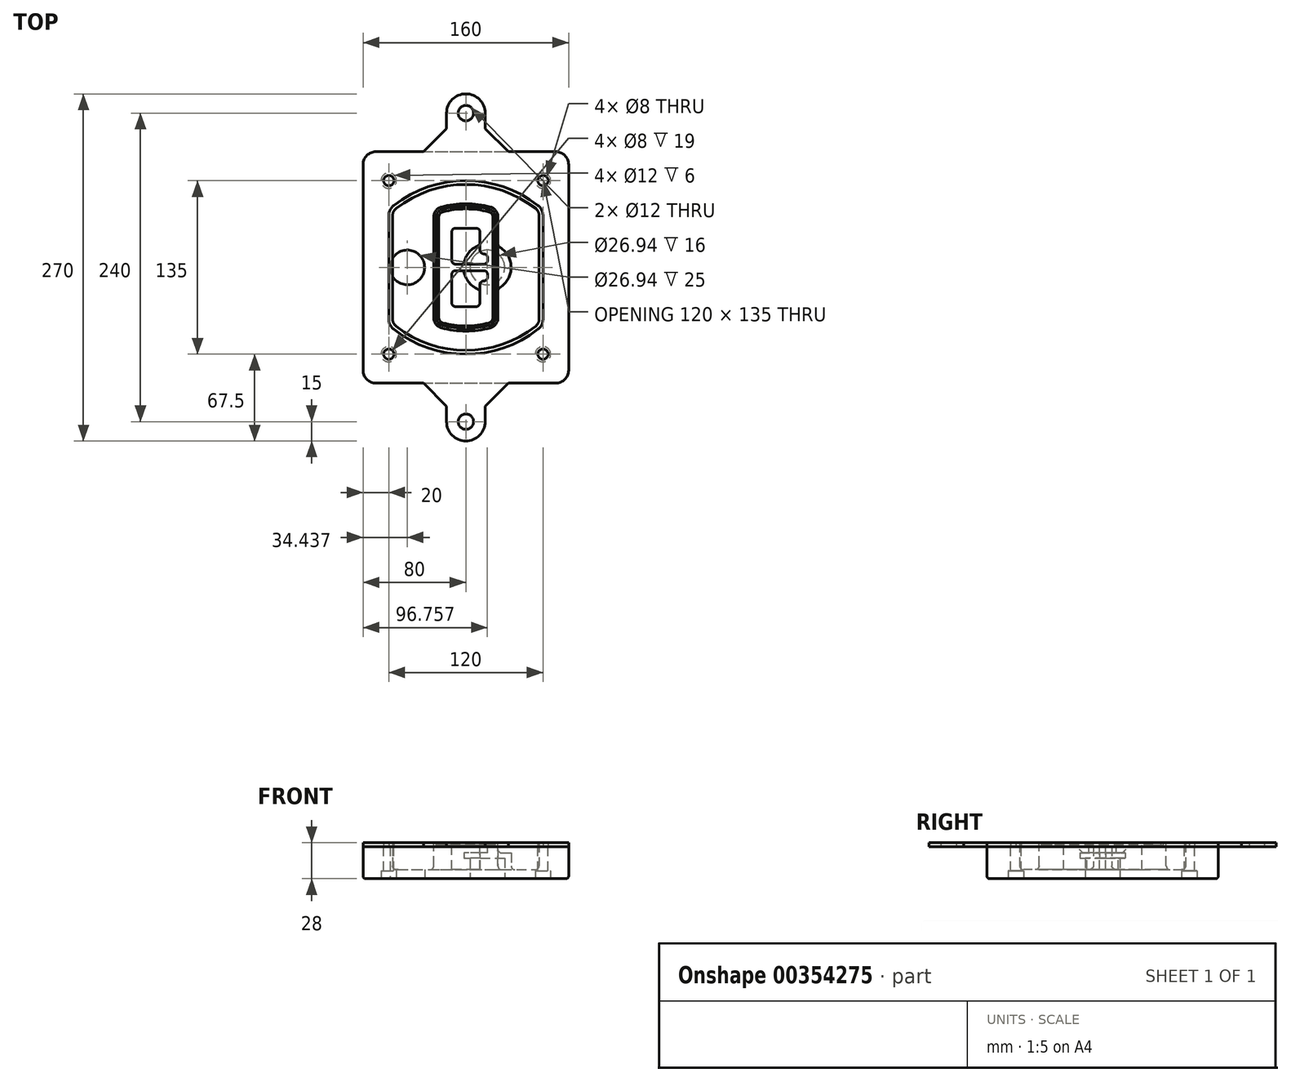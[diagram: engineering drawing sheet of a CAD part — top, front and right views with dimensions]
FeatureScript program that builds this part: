
annotation { "Feature Type Name" : "Feature", "Feature Type Description" : "" }
export const myFeature = defineFeature(function(context is Context, id is Id, definition is map)
    precondition{}
    {
        {
            var Q0;
            Q0=qCreatedBy(makeId("Top.planeOp"),FACE);
            var sketch = newSketch(context, id + "F0", { "sketchPlane" : qUnion([Q0])});
            skPoint(sketch, "E0.rect.middle", {"position": v(0, 0) * mm});
            skLineSegment(sketch, "E1.bottom", {"start": v(-70, -90) * mm, "end": v(70, -90) * mm});
            skLineSegment(sketch, "E1.top", {"start": v(-70, 90) * mm, "end": v(70, 90) * mm});
            skLineSegment(sketch, "E1.left", {"start": v(-80, -80) * mm, "end": v(-80, 80) * mm});
            skLineSegment(sketch, "E1.right", {"start": v(80, -80) * mm, "end": v(80, 80) * mm});
            skLineSegment(sketch, "E2", {"start": v(-80, 90) * mm, "end": v(80, -90) * mm, "construction": true});
            skLineSegment(sketch, "E3", {"start": v(80, 90) * mm, "end": v(-80, -90) * mm, "construction": true});
            skCircle(sketch, "E4", {"center": v(-60, 67.5) * mm, "radius": 4 * mm});
            skCircle(sketch, "E5", {"center": v(60, 67.5) * mm, "radius": 4 * mm});
            skCircle(sketch, "E6", {"center": v(60, -67.5) * mm, "radius": 4 * mm});
            skCircle(sketch, "E7", {"center": v(-60, -67.5) * mm, "radius": 4 * mm});
            skLineSegment(sketch, "E8", {"start": v(-60, 67.5) * mm, "end": v(60, 67.5) * mm, "construction": true});
            skLineSegment(sketch, "E9", {"start": v(60, 67.5) * mm, "end": v(60, -67.5) * mm, "construction": true});
            skLineSegment(sketch, "E10", {"start": v(60, -67.5) * mm, "end": v(-60, -67.5) * mm, "construction": true});
            skLineSegment(sketch, "E11", {"start": v(-60, -67.5) * mm, "end": v(-60, 67.5) * mm, "construction": true});
            skLineSegment(sketch, "E12", {"start": v(-60, 40.3) * mm, "end": v(-60, -40.3) * mm});
            skLineSegment(sketch, "E13", {"start": v(60, 40.3) * mm, "end": v(60, -40.3) * mm});
            skArc(sketch, "E14", {"start": v(56.15, 48.18) * mm, "mid": v(0, 67.5) * mm, "end": v(-56.15, 48.18) * mm});
            skArc(sketch, "E15", {"start": v(-56.15, -48.18) * mm, "mid": v(0, -67.5) * mm, "end": v(56.15, -48.18) * mm});
            skLineSegment(sketch, "E16", {"start": v(-60, 0) * mm, "end": v(60, 0) * mm, "construction": true});
            skPoint(sketch, "E17.visualSharp", {"position": v(-60, -45) * mm});
            skArc(sketch, "E17.filletArc", {"start": v(-60, -40.3) * mm, "mid": v(-58.99, -44.68) * mm, "end": v(-56.15, -48.18) * mm});
            skPoint(sketch, "E18.visualSharp", {"position": v(-60, 45) * mm});
            skArc(sketch, "E18.filletArc", {"start": v(-56.15, 48.18) * mm, "mid": v(-58.99, 44.68) * mm, "end": v(-60, 40.3) * mm});
            skPoint(sketch, "E19.visualSharp", {"position": v(60, 45) * mm});
            skArc(sketch, "E19.filletArc", {"start": v(60, 40.3) * mm, "mid": v(58.99, 44.68) * mm, "end": v(56.15, 48.18) * mm});
            skPoint(sketch, "E20.visualSharp", {"position": v(60, -45) * mm});
            skArc(sketch, "E20.filletArc", {"start": v(56.15, -48.18) * mm, "mid": v(58.99, -44.68) * mm, "end": v(60, -40.3) * mm});
            skPoint(sketch, "E21.visualSharp", {"position": v(-80, 90) * mm});
            skArc(sketch, "E21.filletArc", {"start": v(-70, 90) * mm, "mid": v(-77.07, 87.07) * mm, "end": v(-80, 80) * mm});
            skPoint(sketch, "E22.visualSharp", {"position": v(80, 90) * mm});
            skArc(sketch, "E22.filletArc", {"start": v(80, 80) * mm, "mid": v(77.07, 87.07) * mm, "end": v(70, 90) * mm});
            skPoint(sketch, "E23.visualSharp", {"position": v(80, -90) * mm});
            skArc(sketch, "E23.filletArc", {"start": v(70, -90) * mm, "mid": v(77.07, -87.07) * mm, "end": v(80, -80) * mm});
            skPoint(sketch, "E24.visualSharp", {"position": v(-80, -90) * mm});
            skArc(sketch, "E24.filletArc", {"start": v(-80, -80) * mm, "mid": v(-77.07, -87.07) * mm, "end": v(-70, -90) * mm});
            skArc(sketch, "E25.0", {"start": v(57, 40.3) * mm, "mid": v(56.3, 43.36) * mm, "end": v(54.3, 45.81) * mm});
            skLineSegment(sketch, "E25.1", {"start": v(57, 40.3) * mm, "end": v(57, -40.3) * mm});
            skArc(sketch, "E25.2", {"start": v(54.3, -45.81) * mm, "mid": v(56.3, -43.36) * mm, "end": v(57, -40.3) * mm});
            skArc(sketch, "E25.3", {"start": v(-54.3, -45.81) * mm, "mid": v(0, -64.5) * mm, "end": v(54.3, -45.81) * mm});
            skArc(sketch, "E25.4", {"start": v(-57, -40.3) * mm, "mid": v(-56.3, -43.36) * mm, "end": v(-54.3, -45.81) * mm});
            skArc(sketch, "E25.5", {"start": v(54.3, 45.81) * mm, "mid": v(0, 64.5) * mm, "end": v(-54.3, 45.81) * mm});
            skLineSegment(sketch, "E25.6", {"start": v(-57, 40.3) * mm, "end": v(-57, -40.3) * mm});
            skArc(sketch, "E25.7", {"start": v(-54.3, 45.81) * mm, "mid": v(-56.3, 43.36) * mm, "end": v(-57, 40.3) * mm});
            skArc(sketch, "E26.0", {"start": v(-58.62, 51.33) * mm, "mid": v(-62.58, 46.43) * mm, "end": v(-64, 40.3) * mm});
            skArc(sketch, "E26.1", {"start": v(58.62, 51.33) * mm, "mid": v(0, 71.5) * mm, "end": v(-58.62, 51.33) * mm});
            skArc(sketch, "E26.2", {"start": v(64, 40.3) * mm, "mid": v(62.58, 46.43) * mm, "end": v(58.62, 51.33) * mm});
            skLineSegment(sketch, "E26.3", {"start": v(64, 40.3) * mm, "end": v(64, -40.3) * mm});
            skArc(sketch, "E26.4", {"start": v(58.62, -51.33) * mm, "mid": v(62.58, -46.43) * mm, "end": v(64, -40.3) * mm});
            skLineSegment(sketch, "E26.5", {"start": v(-64, 40.3) * mm, "end": v(-64, -40.3) * mm});
            skArc(sketch, "E26.6", {"start": v(-58.62, -51.33) * mm, "mid": v(0, -71.5) * mm, "end": v(58.62, -51.33) * mm});
            skArc(sketch, "E26.7", {"start": v(-64, -40.3) * mm, "mid": v(-62.58, -46.43) * mm, "end": v(-58.62, -51.33) * mm});
            skSolve(sketch);
        }
        {
            var Q0;
            Q0=makeQuery(id+"F0.imprint","IMPRINT",FACE,{"disambiguationData":[TD([[makeQuery(id+"F0.imprint","IMPRINT",EDGE,{"derivedFrom":sQuery(id+"F0.wireOp",EDGE,"E1.bottom")}),1.0]])]});
            var Q1;
            Q1=makeQuery(id+"F0.imprint","IMPRINT",FACE,{"disambiguationData":[TD([[makeQuery(id+"F0.imprint","IMPRINT",EDGE,{"derivedFrom":sQuery(id+"F0.wireOp",EDGE,"E12")}),1.0]])]});
            var Q2;
            Q2=makeQuery(id+"F0.imprint","IMPRINT",FACE,{"disambiguationData":[TD([[makeQuery(id+"F0.imprint","IMPRINT",EDGE,{"derivedFrom":sQuery(id+"F0.wireOp",EDGE,"E25.0")}),1.0]])]});
            var Q3;
            Q3=makeQuery(id+"F0.imprint","IMPRINT",FACE,{"disambiguationData":[TD([[makeQuery(id+"F0.imprint","IMPRINT",EDGE,{"derivedFrom":sQuery(id+"F0.wireOp",EDGE,"E12")}),-1.0]])]});
            extrude(context, id + "F1", {"entities" : qUnion([Q0, Q1, Q2, Q3]), "oppositeDirection" : true, "depth" : 25 * mm});
        }
        {
            var Q0;
            Q0=makeQuery(id+"F0.imprint","IMPRINT",FACE,{"disambiguationData":[TD([[makeQuery(id+"F0.imprint","IMPRINT",EDGE,{"derivedFrom":sQuery(id+"F0.wireOp",EDGE,"E12")}),1.0]])]});
            extrude(context, id + "F2", {"entities" : qUnion([Q0]), "operationType" : NewBodyOperationType.ADD, "depth" : 3 * mm});
        }
        {
            var Q0;
            Q0=makeQuery(id+"F0.imprint","IMPRINT",FACE,{"disambiguationData":[TD([[makeQuery(id+"F0.imprint","IMPRINT",EDGE,{"derivedFrom":sQuery(id+"F0.wireOp",EDGE,"E25.0")}),1.0]])]});
            extrude(context, id + "F3", {"entities" : qUnion([Q0]), "operationType" : NewBodyOperationType.REMOVE, "oppositeDirection" : true, "depth" : 18 * mm});
        }
        {
            var Q0;
            Q0=makeQuery(id+"F2.opExtrude","CAP_FACE",FACE,{"disambiguationData":[OSD([sQuery(id+"F0.wireOp",EDGE,"E12"),sQuery(id+"F0.wireOp",EDGE,"E13"),sQuery(id+"F0.wireOp",EDGE,"E14"),sQuery(id+"F0.wireOp",EDGE,"E15"),sQuery(id+"F0.wireOp",EDGE,"E17.filletArc"),sQuery(id+"F0.wireOp",EDGE,"E18.filletArc"),sQuery(id+"F0.wireOp",EDGE,"E19.filletArc"),sQuery(id+"F0.wireOp",EDGE,"E20.filletArc"),sQuery(id+"F0.wireOp",EDGE,"E25.0"),sQuery(id+"F0.wireOp",EDGE,"E25.1"),sQuery(id+"F0.wireOp",EDGE,"E25.2"),sQuery(id+"F0.wireOp",EDGE,"E25.3"),sQuery(id+"F0.wireOp",EDGE,"E25.4"),sQuery(id+"F0.wireOp",EDGE,"E25.5"),sQuery(id+"F0.wireOp",EDGE,"E25.6"),sQuery(id+"F0.wireOp",EDGE,"E25.7")])],"isStart":false});
            var sketch = newSketch(context, id + "F4", { "sketchPlane" : qUnion([Q0])});
            skArc(sketch, "E27.0", {"start": v(-19.08, -46.97) * mm, "mid": v(0, -49.5) * mm, "end": v(19.08, -46.97) * mm});
            skArc(sketch, "E28.0", {"start": v(19.08, 46.97) * mm, "mid": v(0, 49.5) * mm, "end": v(-19.08, 46.97) * mm});
            skLineSegment(sketch, "E29", {"start": v(-25, 39.25) * mm, "end": v(-25, -39.25) * mm});
            skLineSegment(sketch, "E30", {"start": v(25, 39.25) * mm, "end": v(25, -39.25) * mm});
            skLineSegment(sketch, "E31", {"start": v(-25, 45.1) * mm, "end": v(25, 45.1) * mm, "construction": true});
            skLineSegment(sketch, "E32", {"start": v(-25, -45.1) * mm, "end": v(25, -45.1) * mm, "construction": true});
            skPoint(sketch, "E33.visualSharp", {"position": v(-25, 45.1) * mm});
            skArc(sketch, "E33.filletArc", {"start": v(-19.08, 46.97) * mm, "mid": v(-23.35, 44.11) * mm, "end": v(-25, 39.25) * mm});
            skPoint(sketch, "E34.visualSharp", {"position": v(25, 45.1) * mm});
            skArc(sketch, "E34.filletArc", {"start": v(25, 39.25) * mm, "mid": v(23.35, 44.11) * mm, "end": v(19.08, 46.97) * mm});
            skPoint(sketch, "E35.visualSharp", {"position": v(25, -45.1) * mm});
            skArc(sketch, "E35.filletArc", {"start": v(19.08, -46.97) * mm, "mid": v(23.35, -44.11) * mm, "end": v(25, -39.25) * mm});
            skPoint(sketch, "E36.visualSharp", {"position": v(-25, -45.1) * mm});
            skArc(sketch, "E36.filletArc", {"start": v(-25, -39.25) * mm, "mid": v(-23.35, -44.11) * mm, "end": v(-19.08, -46.97) * mm});
            skArc(sketch, "E37.0", {"start": v(54.3, 45.81) * mm, "mid": v(0, 64.5) * mm, "end": v(-54.3, 45.81) * mm});
            skArc(sketch, "E37.1", {"start": v(-54.3, 45.81) * mm, "mid": v(-56.3, 43.36) * mm, "end": v(-57, 40.3) * mm});
            skLineSegment(sketch, "E37.2", {"start": v(-57, 40.3) * mm, "end": v(-57, -40.3) * mm});
            skArc(sketch, "E37.3", {"start": v(-57, -40.3) * mm, "mid": v(-56.3, -43.36) * mm, "end": v(-54.3, -45.81) * mm});
            skArc(sketch, "E37.4", {"start": v(-54.3, -45.81) * mm, "mid": v(0, -64.5) * mm, "end": v(54.3, -45.81) * mm});
            skArc(sketch, "E37.5", {"start": v(54.3, -45.81) * mm, "mid": v(56.3, -43.36) * mm, "end": v(57, -40.3) * mm});
            skLineSegment(sketch, "E37.6", {"start": v(57, 40.3) * mm, "end": v(57, -40.3) * mm});
            skArc(sketch, "E37.7", {"start": v(57, 40.3) * mm, "mid": v(56.3, 43.36) * mm, "end": v(54.3, 45.81) * mm});
            skLineSegment(sketch, "E38.0", {"start": v(23, 39.25) * mm, "end": v(23, -39.25) * mm});
            skArc(sketch, "E38.1", {"start": v(18.56, -45.04) * mm, "mid": v(21.76, -42.9) * mm, "end": v(23, -39.25) * mm});
            skArc(sketch, "E38.2", {"start": v(-18.56, -45.04) * mm, "mid": v(0, -47.5) * mm, "end": v(18.56, -45.04) * mm});
            skArc(sketch, "E38.3", {"start": v(-23, -39.25) * mm, "mid": v(-21.76, -42.9) * mm, "end": v(-18.56, -45.04) * mm});
            skLineSegment(sketch, "E38.4", {"start": v(-23, 39.25) * mm, "end": v(-23, -39.25) * mm});
            skArc(sketch, "E38.5", {"start": v(23, 39.25) * mm, "mid": v(21.76, 42.9) * mm, "end": v(18.56, 45.04) * mm});
            skArc(sketch, "E38.6", {"start": v(-18.56, 45.04) * mm, "mid": v(-21.76, 42.9) * mm, "end": v(-23, 39.25) * mm});
            skArc(sketch, "E38.7", {"start": v(18.56, 45.04) * mm, "mid": v(0, 47.5) * mm, "end": v(-18.56, 45.04) * mm});
            skArc(sketch, "E39.0", {"start": v(21, 39.25) * mm, "mid": v(20.18, 41.68) * mm, "end": v(18.04, 43.1) * mm});
            skLineSegment(sketch, "E39.1", {"start": v(21, 39.25) * mm, "end": v(21, -39.25) * mm});
            skArc(sketch, "E39.2", {"start": v(18.04, -43.1) * mm, "mid": v(20.18, -41.68) * mm, "end": v(21, -39.25) * mm});
            skArc(sketch, "E39.3", {"start": v(-18.04, -43.1) * mm, "mid": v(0, -45.5) * mm, "end": v(18.04, -43.1) * mm});
            skArc(sketch, "E39.4", {"start": v(-21, -39.25) * mm, "mid": v(-20.18, -41.68) * mm, "end": v(-18.04, -43.1) * mm});
            skArc(sketch, "E39.5", {"start": v(18.04, 43.1) * mm, "mid": v(0, 45.5) * mm, "end": v(-18.04, 43.1) * mm});
            skLineSegment(sketch, "E39.6", {"start": v(-21, 39.25) * mm, "end": v(-21, -39.25) * mm});
            skArc(sketch, "E39.7", {"start": v(-18.04, 43.1) * mm, "mid": v(-20.18, 41.68) * mm, "end": v(-21, 39.25) * mm});
            skLineSegment(sketch, "E40", {"start": v(-25, 0) * mm, "end": v(25, 0) * mm, "construction": true});
            skLineSegment(sketch, "E41", {"start": v(-11, 5.5) * mm, "end": v(-11, 27.5) * mm});
            skLineSegment(sketch, "E42", {"start": v(-8, 30.5) * mm, "end": v(8, 30.5) * mm});
            skLineSegment(sketch, "E43", {"start": v(11, 27.5) * mm, "end": v(11, 13.5) * mm});
            skLineSegment(sketch, "E44", {"start": v(14, 10.5) * mm, "end": v(14, 10.5) * mm});
            skLineSegment(sketch, "E45", {"start": v(17, 7.5) * mm, "end": v(17, 5.5) * mm});
            skLineSegment(sketch, "E46", {"start": v(14, 2.5) * mm, "end": v(-8, 2.5) * mm});
            skPoint(sketch, "E47.visualSharp", {"position": v(-11, 30.5) * mm});
            skArc(sketch, "E47.filletArc", {"start": v(-8, 30.5) * mm, "mid": v(-10.12, 29.62) * mm, "end": v(-11, 27.5) * mm});
            skPoint(sketch, "E48.visualSharp", {"position": v(11, 30.5) * mm});
            skArc(sketch, "E48.filletArc", {"start": v(11, 27.5) * mm, "mid": v(10.12, 29.62) * mm, "end": v(8, 30.5) * mm});
            skPoint(sketch, "E49.visualSharp", {"position": v(11, 10.5) * mm});
            skArc(sketch, "E49.filletArc", {"start": v(11, 13.5) * mm, "mid": v(11.88, 11.38) * mm, "end": v(14, 10.5) * mm});
            skPoint(sketch, "E50.visualSharp", {"position": v(17, 10.5) * mm});
            skArc(sketch, "E50.filletArc", {"start": v(17, 7.5) * mm, "mid": v(16.12, 9.62) * mm, "end": v(14, 10.5) * mm});
            skPoint(sketch, "E51.visualSharp", {"position": v(17, 2.5) * mm});
            skArc(sketch, "E51.filletArc", {"start": v(14, 2.5) * mm, "mid": v(16.12, 3.38) * mm, "end": v(17, 5.5) * mm});
            skPoint(sketch, "E52.visualSharp", {"position": v(-11, 2.5) * mm});
            skArc(sketch, "E52.filletArc", {"start": v(-11, 5.5) * mm, "mid": v(-10.12, 3.38) * mm, "end": v(-8, 2.5) * mm});
            skLineSegment(sketch, "E53.0.MirrorCS", {"start": v(14, -2.5) * mm, "end": v(-8, -2.5) * mm});
            skArc(sketch, "E54.0.MirrorCS", {"start": v(-11, -5.5) * mm, "mid": v(-10.12, -3.38) * mm, "end": v(-8, -2.5) * mm});
            skLineSegment(sketch, "E55.0.MirrorCS", {"start": v(-11, -5.5) * mm, "end": v(-11, -27.5) * mm});
            skArc(sketch, "E56.0.MirrorCS", {"start": v(-8, -30.5) * mm, "mid": v(-10.12, -29.62) * mm, "end": v(-11, -27.5) * mm});
            skLineSegment(sketch, "E57.0.MirrorCS", {"start": v(-8, -30.5) * mm, "end": v(8, -30.5) * mm});
            skArc(sketch, "E58.0.MirrorCS", {"start": v(11, -27.5) * mm, "mid": v(10.12, -29.62) * mm, "end": v(8, -30.5) * mm});
            skLineSegment(sketch, "E59.0.MirrorCS", {"start": v(11, -27.5) * mm, "end": v(11, -13.5) * mm});
            skArc(sketch, "E60.0.MirrorCS", {"start": v(11, -13.5) * mm, "mid": v(11.88, -11.38) * mm, "end": v(14, -10.5) * mm});
            skArc(sketch, "E61.0.MirrorCS", {"start": v(17, -7.5) * mm, "mid": v(16.12, -9.62) * mm, "end": v(14, -10.5) * mm});
            skLineSegment(sketch, "E62.0.MirrorCS", {"start": v(17, -7.5) * mm, "end": v(17, -5.5) * mm});
            skArc(sketch, "E63.0.MirrorCS", {"start": v(14, -2.5) * mm, "mid": v(16.12, -3.38) * mm, "end": v(17, -5.5) * mm});
            skSolve(sketch);
        }
        {
            var Q0;
            Q0=makeQuery(id+"F4.imprint","IMPRINT",FACE,{"disambiguationData":[TD([[makeQuery(id+"F4.imprint","IMPRINT",EDGE,{"derivedFrom":sQuery(id+"F4.wireOp",EDGE,"E27.0")}),1.0]])]});
            var Q1;
            Q1=makeQuery(id+"F4.imprint","IMPRINT",FACE,{"disambiguationData":[TD([[makeQuery(id+"F4.imprint","IMPRINT",EDGE,{"derivedFrom":sQuery(id+"F4.wireOp",EDGE,"E38.0")}),-1.0]])]});
            var Q2;
            Q2=makeQuery(id+"F4.imprint","IMPRINT",FACE,{"disambiguationData":[TD([[makeQuery(id+"F4.imprint","IMPRINT",EDGE,{"derivedFrom":sQuery(id+"F4.wireOp",EDGE,"E39.0")}),1.0]])]});
            extrude(context, id + "F5", {"entities" : qUnion([Q0, Q1, Q2]), "operationType" : NewBodyOperationType.ADD, "endBound" : BoundingType.UP_TO_NEXT, "oppositeDirection" : true, "depth" : 25 * mm});
        }
        {
            var Q0;
            Q0=makeQuery(id+"F4.imprint","IMPRINT",FACE,{"disambiguationData":[TD([[makeQuery(id+"F4.imprint","IMPRINT",EDGE,{"derivedFrom":sQuery(id+"F4.wireOp",EDGE,"E38.0")}),-1.0]])]});
            extrude(context, id + "F6", {"entities" : qUnion([Q0]), "operationType" : NewBodyOperationType.REMOVE, "oppositeDirection" : true, "depth" : 2 * mm});
        }
        {
            var Q0;
            Q0=makeQuery(id+"F1.opExtrude","CAP_FACE",FACE,{"disambiguationData":[OSD([sQuery(id+"F0.wireOp",EDGE,"E1.bottom"),sQuery(id+"F0.wireOp",EDGE,"E1.top"),sQuery(id+"F0.wireOp",EDGE,"E1.left"),sQuery(id+"F0.wireOp",EDGE,"E1.right"),sQuery(id+"F0.wireOp",EDGE,"E4"),sQuery(id+"F0.wireOp",EDGE,"E5"),sQuery(id+"F0.wireOp",EDGE,"E6"),sQuery(id+"F0.wireOp",EDGE,"E7"),sQuery(id+"F0.wireOp",EDGE,"E21.filletArc"),sQuery(id+"F0.wireOp",EDGE,"E22.filletArc"),sQuery(id+"F0.wireOp",EDGE,"E23.filletArc"),sQuery(id+"F0.wireOp",EDGE,"E24.filletArc")])],"isStart":false});
            var sketch = newSketch(context, id + "F7", { "sketchPlane" : qUnion([Q0])});
            skCircle(sketch, "E64", {"center": v(16.76, 0) * mm, "radius": 13.47 * mm});
            skCircle(sketch, "E65", {"center": v(-45.56, 0) * mm, "radius": 13.47 * mm});
            skLineSegment(sketch, "E66", {"start": v(80, 0) * mm, "end": v(-80, 0) * mm});
            skCircle(sketch, "E67", {"center": v(16.76, 0) * mm, "radius": 18.47 * mm});
            skCircle(sketch, "E68", {"center": v(60, -67.5) * mm, "radius": 6 * mm});
            skCircle(sketch, "E69", {"center": v(-60, -67.5) * mm, "radius": 6 * mm});
            skCircle(sketch, "E70", {"center": v(-60, 67.5) * mm, "radius": 6 * mm});
            skCircle(sketch, "E71", {"center": v(60, 67.5) * mm, "radius": 6 * mm});
            skSolve(sketch);
        }
        {
            var Q0;
            {var subQ1=sQuery(id+"F7.wireOp",EDGE,"E66");var subQ4=sQuery(id+"F7.wireOp",EDGE,"E64");var subQ6=makeQuery(id+"F7.imprint","INTERSECT",VERTEX,{"disambiguationData":[OD(0.0)],"derivedFrom":[subQ4,subQ1]});Q0=makeQuery(id+"F7.imprint","IMPRINT",FACE,{"disambiguationData":[TD([[makeQuery(id+"F7.imprint","IMPRINT",EDGE,{"disambiguationData":[TD([[subQ6,-1.0]])],"derivedFrom":subQ4}),-1.0]])]});}
            var Q1;
            {var subQ0=sQuery(id+"F7.wireOp",EDGE,"E66");var subQ1=sQuery(id+"F7.wireOp",EDGE,"E64");var subQ3=makeQuery(id+"F7.imprint","INTERSECT",VERTEX,{"disambiguationData":[OD(0.0)],"derivedFrom":[subQ1,subQ0]});Q1=makeQuery(id+"F7.imprint","IMPRINT",FACE,{"disambiguationData":[TD([[makeQuery(id+"F7.imprint","IMPRINT",EDGE,{"disambiguationData":[TD([[subQ3,-1.0]])],"derivedFrom":subQ1}),1.0]])]});}
            var Q2;
            {var subQ0=sQuery(id+"F7.wireOp",EDGE,"E66");var subQ1=sQuery(id+"F7.wireOp",EDGE,"E64");var subQ3=makeQuery(id+"F7.imprint","INTERSECT",VERTEX,{"disambiguationData":[OD(0.0)],"derivedFrom":[subQ1,subQ0]});Q2=makeQuery(id+"F7.imprint","IMPRINT",FACE,{"disambiguationData":[TD([[makeQuery(id+"F7.imprint","IMPRINT",EDGE,{"disambiguationData":[TD([[subQ3,1.0]])],"derivedFrom":subQ1}),1.0]])]});}
            var Q3;
            {var subQ1=sQuery(id+"F7.wireOp",EDGE,"E66");var subQ4=sQuery(id+"F7.wireOp",EDGE,"E64");var subQ6=makeQuery(id+"F7.imprint","INTERSECT",VERTEX,{"disambiguationData":[OD(0.0)],"derivedFrom":[subQ4,subQ1]});Q3=makeQuery(id+"F7.imprint","IMPRINT",FACE,{"disambiguationData":[TD([[makeQuery(id+"F7.imprint","IMPRINT",EDGE,{"disambiguationData":[TD([[subQ6,1.0]])],"derivedFrom":subQ4}),-1.0]])]});}
            extrude(context, id + "F8", {"entities" : qUnion([Q0, Q1, Q2, Q3]), "operationType" : NewBodyOperationType.ADD, "oppositeDirection" : true, "depth" : 20 * mm});
        }
        {
            var Q0;
            {var subQ0=sQuery(id+"F7.wireOp",EDGE,"E66");var subQ1=sQuery(id+"F7.wireOp",EDGE,"E64");var subQ3=makeQuery(id+"F7.imprint","INTERSECT",VERTEX,{"disambiguationData":[OD(0.0)],"derivedFrom":[subQ1,subQ0]});Q0=makeQuery(id+"F7.imprint","IMPRINT",FACE,{"disambiguationData":[TD([[makeQuery(id+"F7.imprint","IMPRINT",EDGE,{"disambiguationData":[TD([[subQ3,-1.0]])],"derivedFrom":subQ1}),1.0]])]});}
            var Q1;
            {var subQ0=sQuery(id+"F7.wireOp",EDGE,"E66");var subQ1=sQuery(id+"F7.wireOp",EDGE,"E64");var subQ3=makeQuery(id+"F7.imprint","INTERSECT",VERTEX,{"disambiguationData":[OD(0.0)],"derivedFrom":[subQ1,subQ0]});Q1=makeQuery(id+"F7.imprint","IMPRINT",FACE,{"disambiguationData":[TD([[makeQuery(id+"F7.imprint","IMPRINT",EDGE,{"disambiguationData":[TD([[subQ3,1.0]])],"derivedFrom":subQ1}),1.0]])]});}
            extrude(context, id + "F9", {"entities" : qUnion([Q0, Q1]), "operationType" : NewBodyOperationType.REMOVE, "oppositeDirection" : true, "depth" : 16 * mm});
        }
        {
            var Q0;
            {var subQ0=sQuery(id+"F7.wireOp",EDGE,"E66");var subQ1=sQuery(id+"F7.wireOp",EDGE,"E65");var subQ3=makeQuery(id+"F7.imprint","INTERSECT",VERTEX,{"disambiguationData":[OD(0.0)],"derivedFrom":[subQ1,subQ0]});Q0=makeQuery(id+"F7.imprint","IMPRINT",FACE,{"disambiguationData":[TD([[makeQuery(id+"F7.imprint","IMPRINT",EDGE,{"disambiguationData":[TD([[subQ3,-1.0]])],"derivedFrom":subQ1}),1.0]])]});}
            var Q1;
            {var subQ0=sQuery(id+"F7.wireOp",EDGE,"E66");var subQ1=sQuery(id+"F7.wireOp",EDGE,"E65");var subQ3=makeQuery(id+"F7.imprint","INTERSECT",VERTEX,{"disambiguationData":[OD(0.0)],"derivedFrom":[subQ1,subQ0]});Q1=makeQuery(id+"F7.imprint","IMPRINT",FACE,{"disambiguationData":[TD([[makeQuery(id+"F7.imprint","IMPRINT",EDGE,{"disambiguationData":[TD([[subQ3,1.0]])],"derivedFrom":subQ1}),1.0]])]});}
            extrude(context, id + "F10", {"entities" : qUnion([Q0, Q1]), "operationType" : NewBodyOperationType.REMOVE, "oppositeDirection" : true, "depth" : 25 * mm});
        }
        {
            var Q0;
            Q0=makeQuery(id+"F7.imprint","IMPRINT",FACE,{"disambiguationData":[TD([[makeQuery(id+"F7.imprint","IMPRINT",EDGE,{"derivedFrom":sQuery(id+"F7.wireOp",EDGE,"E68")}),1.0]])]});
            var Q1;
            Q1=makeQuery(id+"F7.imprint","IMPRINT",FACE,{"disambiguationData":[TD([[makeQuery(id+"F7.imprint","IMPRINT",EDGE,{"derivedFrom":makeQuery(id+"F1.opExtrude","CAP_EDGE",EDGE,{"disambiguationData":[OSD([sQuery(id+"F0.wireOp",EDGE,"E5")])],"isStart":false})}),-1.0]])]});
            var Q2;
            Q2=makeQuery(id+"F7.imprint","IMPRINT",FACE,{"disambiguationData":[TD([[makeQuery(id+"F7.imprint","IMPRINT",EDGE,{"derivedFrom":sQuery(id+"F7.wireOp",EDGE,"E69")}),1.0]])]});
            var Q3;
            Q3=makeQuery(id+"F7.imprint","IMPRINT",FACE,{"disambiguationData":[TD([[makeQuery(id+"F7.imprint","IMPRINT",EDGE,{"derivedFrom":makeQuery(id+"F1.opExtrude","CAP_EDGE",EDGE,{"disambiguationData":[OSD([sQuery(id+"F0.wireOp",EDGE,"E4")])],"isStart":false})}),-1.0]])]});
            var Q4;
            Q4=makeQuery(id+"F7.imprint","IMPRINT",FACE,{"disambiguationData":[TD([[makeQuery(id+"F7.imprint","IMPRINT",EDGE,{"derivedFrom":sQuery(id+"F7.wireOp",EDGE,"E70")}),1.0]])]});
            var Q5;
            Q5=makeQuery(id+"F7.imprint","IMPRINT",FACE,{"disambiguationData":[TD([[makeQuery(id+"F7.imprint","IMPRINT",EDGE,{"derivedFrom":makeQuery(id+"F1.opExtrude","CAP_EDGE",EDGE,{"disambiguationData":[OSD([sQuery(id+"F0.wireOp",EDGE,"E7")])],"isStart":false})}),-1.0]])]});
            var Q6;
            Q6=makeQuery(id+"F7.imprint","IMPRINT",FACE,{"disambiguationData":[TD([[makeQuery(id+"F7.imprint","IMPRINT",EDGE,{"derivedFrom":sQuery(id+"F7.wireOp",EDGE,"E71")}),1.0]])]});
            var Q7;
            Q7=makeQuery(id+"F7.imprint","IMPRINT",FACE,{"disambiguationData":[TD([[makeQuery(id+"F7.imprint","IMPRINT",EDGE,{"derivedFrom":makeQuery(id+"F1.opExtrude","CAP_EDGE",EDGE,{"disambiguationData":[OSD([sQuery(id+"F0.wireOp",EDGE,"E6")])],"isStart":false})}),-1.0]])]});
            extrude(context, id + "F11", {"entities" : qUnion([Q0, Q1, Q2, Q3, Q4, Q5, Q6, Q7]), "operationType" : NewBodyOperationType.REMOVE, "oppositeDirection" : true, "depth" : 6 * mm});
        }
        {
            var Q0;
            Q0=makeQuery(id+"F9.boolean.opBoolean","COPY",FACE,{"derivedFrom":makeQuery(id+"F9.opExtrude","CAP_FACE",FACE,{"disambiguationData":[OSD([sQuery(id+"F7.wireOp",EDGE,"E64")])],"isStart":false})});
            var sketch = newSketch(context, id + "F12", { "sketchPlane" : qUnion([Q0])});
            skArc(sketch, "E72.0", {"start": v(11, 17.55) * mm, "mid": v(2.57, 11.82) * mm, "end": v(-1.54, 2.5) * mm});
            skArc(sketch, "E72.1", {"start": v(-1.54, -2.5) * mm, "mid": v(2.57, -11.82) * mm, "end": v(11, -17.55) * mm});
            skLineSegment(sketch, "E73", {"start": v(-1.54, -2.5) * mm, "end": v(14, -2.5) * mm});
            skLineSegment(sketch, "E74.0", {"start": v(14, 2.5) * mm, "end": v(-1.54, 2.5) * mm});
            skArc(sketch, "E74.1", {"start": v(14, 2.5) * mm, "mid": v(16.12, 3.38) * mm, "end": v(17, 5.5) * mm});
            skLineSegment(sketch, "E74.2", {"start": v(17, 7.5) * mm, "end": v(17, 5.5) * mm});
            skArc(sketch, "E74.3", {"start": v(17, 7.5) * mm, "mid": v(16.12, 9.62) * mm, "end": v(14, 10.5) * mm});
            skArc(sketch, "E74.4", {"start": v(11, 13.5) * mm, "mid": v(11.88, 11.38) * mm, "end": v(14, 10.5) * mm});
            skLineSegment(sketch, "E74.5", {"start": v(11, 17.55) * mm, "end": v(11, 13.5) * mm});
            skLineSegment(sketch, "E74.7", {"start": v(14, -2.5) * mm, "end": v(-1.54, -2.5) * mm});
            skArc(sketch, "E74.8", {"start": v(14, -2.5) * mm, "mid": v(16.12, -3.38) * mm, "end": v(17, -5.5) * mm});
            skLineSegment(sketch, "E74.9", {"start": v(17, -7.5) * mm, "end": v(17, -5.5) * mm});
            skArc(sketch, "E74.10", {"start": v(17, -7.5) * mm, "mid": v(16.12, -9.62) * mm, "end": v(14, -10.5) * mm});
            skArc(sketch, "E74.11", {"start": v(11, -13.5) * mm, "mid": v(11.88, -11.38) * mm, "end": v(14, -10.5) * mm});
            skLineSegment(sketch, "E74.12", {"start": v(11, -17.55) * mm, "end": v(11, -13.5) * mm});
            skPoint(sketch, "E75.orphan", {"position": v(11, -27.5) * mm});
            skPoint(sketch, "E76.orphan", {"position": v(-8, -2.5) * mm});
            skPoint(sketch, "E77.orphan", {"position": v(-8, 2.5) * mm});
            skPoint(sketch, "E78.orphan", {"position": v(11, 27.5) * mm});
            skSolve(sketch);
        }
        {
            var Q0;
            {var subQ7=sQuery(id+"F12.wireOp",EDGE,"E72.0");var subQ14=sQuery(id+"F12.wireOp",EDGE,"E72.1");var subQ16=sQuery(id+"F12.wireOp",EDGE,"E74.1");var subQ18=sQuery(id+"F12.wireOp",EDGE,"E74.8");Q0=qUnion([makeQuery(id+"F12.imprint","IMPRINT",FACE,{"disambiguationData":[TD([[makeQuery(id+"F12.imprint","IMPRINT",EDGE,{"derivedFrom":subQ7}),1.0]])]}),makeQuery(id+"F12.imprint","IMPRINT",FACE,{"disambiguationData":[TD([[makeQuery(id+"F12.imprint","IMPRINT",EDGE,{"derivedFrom":subQ14}),1.0]])]}),makeQuery(id+"F12.imprint","IMPRINT",FACE,{"disambiguationData":[TD([[makeQuery(id+"F12.imprint","IMPRINT",EDGE,{"derivedFrom":subQ16}),1.0]])]}),makeQuery(id+"F12.imprint","IMPRINT",FACE,{"disambiguationData":[TD([[makeQuery(id+"F12.imprint","IMPRINT",EDGE,{"derivedFrom":subQ18}),-1.0]])]})]);}
            var Q1;
            Q1=makeQuery(id+"F5.boolean.opBoolean","SPLIT",FACE,{"disambiguationData":[TD([makeQuery(id+"F5.opExtrude","SWEPT_FACE",FACE,{"disambiguationData":[OSD([sQuery(id+"F4.wireOp",EDGE,"E41")])]})])],"derivedFrom":makeQuery(id+"F3.boolean.opBoolean","COPY",FACE,{"derivedFrom":makeQuery(id+"F3.opExtrude","CAP_FACE",FACE,{"disambiguationData":[OSD([sQuery(id+"F0.wireOp",EDGE,"E25.0"),sQuery(id+"F0.wireOp",EDGE,"E25.1"),sQuery(id+"F0.wireOp",EDGE,"E25.2"),sQuery(id+"F0.wireOp",EDGE,"E25.3"),sQuery(id+"F0.wireOp",EDGE,"E25.4"),sQuery(id+"F0.wireOp",EDGE,"E25.5"),sQuery(id+"F0.wireOp",EDGE,"E25.6"),sQuery(id+"F0.wireOp",EDGE,"E25.7")])],"isStart":false})})});
            extrude(context, id + "F13", {"entities" : qUnion([Q0]), "operationType" : NewBodyOperationType.REMOVE, "endBound" : BoundingType.UP_TO_SURFACE, "endBoundEntityFace" : qUnion([Q1]), "depth" : 25 * mm});
        }
        {
            var Q0;
            Q0=makeQuery(id+"F3.boolean.opBoolean","COPY",EDGE,{"derivedFrom":makeQuery(id+"F3.opExtrude","CAP_EDGE",EDGE,{"disambiguationData":[OSD([sQuery(id+"F0.wireOp",EDGE,"E25.6")])],"isStart":false})});
            var Q1;
            Q1=makeQuery(id+"F8.boolean.opBoolean","INTERSECT",EDGE,{"derivedFrom":[makeQuery(id+"F5.opExtrude","SWEPT_FACE",FACE,{"disambiguationData":[OSD([sQuery(id+"F4.wireOp",EDGE,"E30")])]}),makeQuery(id+"F8.opExtrude","CAP_FACE",FACE,{"disambiguationData":[OSD([sQuery(id+"F7.wireOp",EDGE,"E67")])],"isStart":false})]});
            var Q2;
            Q2=makeQuery(id+"F8.boolean.opBoolean","INTERSECT",EDGE,{"disambiguationData":[OD(1.0)],"derivedFrom":[makeQuery(id+"F5.opExtrude","SWEPT_FACE",FACE,{"disambiguationData":[OSD([sQuery(id+"F4.wireOp",EDGE,"E30")])]}),makeQuery(id+"F8.opExtrude","SWEPT_FACE",FACE,{"disambiguationData":[OSD([sQuery(id+"F7.wireOp",EDGE,"E67")])]})]});
            var Q3;
            {var subQ0=sQuery(id+"F4.wireOp",EDGE,"E30");Q3=makeQuery(id+"F8.boolean.opBoolean","SPLIT",EDGE,{"disambiguationData":[TD([makeQuery(id+"F5.opExtrude","SWEPT_FACE",FACE,{"disambiguationData":[OSD([sQuery(id+"F4.wireOp",EDGE,"E35.filletArc")])]})])],"derivedFrom":makeQuery(id+"F5.opExtrude","CAP_EDGE",EDGE,{"disambiguationData":[OSD([subQ0])],"isStart":false})});}
            var Q4;
            {var subQ0=sQuery(id+"F0.wireOp",EDGE,"E25.7");var subQ1=sQuery(id+"F0.wireOp",EDGE,"E25.1");var subQ2=sQuery(id+"F0.wireOp",EDGE,"E25.6");var subQ3=sQuery(id+"F0.wireOp",EDGE,"E25.5");var subQ4=sQuery(id+"F0.wireOp",EDGE,"E25.4");var subQ5=sQuery(id+"F0.wireOp",EDGE,"E25.0");var subQ6=sQuery(id+"F0.wireOp",EDGE,"E25.2");var subQ7=sQuery(id+"F0.wireOp",EDGE,"E25.3");Q4=makeQuery(id+"F8.boolean.opBoolean","INTERSECT",EDGE,{"derivedFrom":[makeQuery(id+"F5.boolean.opBoolean","SPLIT",FACE,{"disambiguationData":[TD([makeQuery(id+"F2.opExtrude","SWEPT_FACE",FACE,{"disambiguationData":[OSD([subQ5])]})])],"derivedFrom":makeQuery(id+"F3.boolean.opBoolean","COPY",FACE,{"derivedFrom":makeQuery(id+"F3.opExtrude","CAP_FACE",FACE,{"disambiguationData":[OSD([subQ5,subQ1,subQ6,subQ7,subQ4,subQ3,subQ2,subQ0])],"isStart":false})})}),makeQuery(id+"F8.opExtrude","SWEPT_FACE",FACE,{"disambiguationData":[OSD([sQuery(id+"F7.wireOp",EDGE,"E67")])]})]});}
            var Q5;
            Q5=makeQuery(id+"F8.boolean.opBoolean","INTERSECT",EDGE,{"disambiguationData":[OD(0.0)],"derivedFrom":[makeQuery(id+"F5.opExtrude","SWEPT_FACE",FACE,{"disambiguationData":[OSD([sQuery(id+"F4.wireOp",EDGE,"E30")])]}),makeQuery(id+"F8.opExtrude","SWEPT_FACE",FACE,{"disambiguationData":[OSD([sQuery(id+"F7.wireOp",EDGE,"E67")])]})]});
            fillet(context, id + "F14", {"entities" : qUnion([Q0, Q1, Q2, Q3, Q4, Q5]), "radius" : 3 * mm, "tangentPropagation" : true, "allowEdgeOverflow" : false});
        }
        {
            var Q0;
            Q0=makeQuery(id+"F1.opExtrude","CAP_EDGE",EDGE,{"disambiguationData":[OSD([sQuery(id+"F0.wireOp",EDGE,"E1.bottom")])],"isStart":false});
            fillet(context, id + "F15", {"entities" : qUnion([Q0]), "radius" : 2 * mm, "tangentPropagation" : true, "allowEdgeOverflow" : false});
        }
        {
            var Q0;
            {var subQ0=sQuery(id+"F0.wireOp",EDGE,"E21.filletArc");var subQ1=sQuery(id+"F0.wireOp",EDGE,"E7");var subQ2=sQuery(id+"F0.wireOp",EDGE,"E6");var subQ3=sQuery(id+"F0.wireOp",EDGE,"E5");var subQ4=sQuery(id+"F0.wireOp",EDGE,"E4");var subQ5=sQuery(id+"F0.wireOp",EDGE,"E22.filletArc");var subQ6=sQuery(id+"F0.wireOp",EDGE,"E1.bottom");var subQ7=sQuery(id+"F0.wireOp",EDGE,"E1.right");var subQ8=sQuery(id+"F0.wireOp",EDGE,"E1.top");var subQ9=sQuery(id+"F0.wireOp",EDGE,"E1.left");var subQ10=sQuery(id+"F0.wireOp",EDGE,"E23.filletArc");var subQ11=sQuery(id+"F0.wireOp",EDGE,"E24.filletArc");Q0=makeQuery(id+"F2.boolean.opBoolean","SPLIT",FACE,{"disambiguationData":[TD([makeQuery(id+"F1.opExtrude","SWEPT_FACE",FACE,{"disambiguationData":[OSD([subQ6])]})])],"derivedFrom":makeQuery(id+"F1.opExtrude","CAP_FACE",FACE,{"disambiguationData":[OSD([subQ6,subQ8,subQ9,subQ7,subQ4,subQ3,subQ2,subQ1,subQ0,subQ5,subQ10,subQ11])],"isStart":true})});}
            var sketch = newSketch(context, id + "F16", { "sketchPlane" : qUnion([Q0])});
            skLineSegment(sketch, "E79.0", {"start": v(-70, 90) * mm, "end": v(70, 90) * mm});
            skArc(sketch, "E79.1", {"start": v(-70, 90) * mm, "mid": v(-77.07, 87.07) * mm, "end": v(-80, 80) * mm});
            skLineSegment(sketch, "E79.2", {"start": v(-80, -80) * mm, "end": v(-80, 80) * mm});
            skArc(sketch, "E79.3", {"start": v(80, 80) * mm, "mid": v(77.07, 87.07) * mm, "end": v(70, 90) * mm});
            skLineSegment(sketch, "E79.4", {"start": v(80, -80) * mm, "end": v(80, 80) * mm});
            skArc(sketch, "E79.5", {"start": v(70, -90) * mm, "mid": v(77.07, -87.07) * mm, "end": v(80, -80) * mm});
            skLineSegment(sketch, "E79.6", {"start": v(-70, -90) * mm, "end": v(70, -90) * mm});
            skArc(sketch, "E79.7", {"start": v(-80, -80) * mm, "mid": v(-77.07, -87.07) * mm, "end": v(-70, -90) * mm});
            skPoint(sketch, "E79.8", {"position": v(-80, 0) * mm});
            skArc(sketch, "E80.0", {"start": v(56.15, 48.18) * mm, "mid": v(0, 67.5) * mm, "end": v(-56.15, 48.18) * mm});
            skLineSegment(sketch, "E80.1", {"start": v(60, 40.3) * mm, "end": v(60, -40.3) * mm});
            skArc(sketch, "E80.2", {"start": v(60, 40.3) * mm, "mid": v(58.99, 44.68) * mm, "end": v(56.15, 48.18) * mm});
            skArc(sketch, "E80.3", {"start": v(56.15, -48.18) * mm, "mid": v(58.99, -44.68) * mm, "end": v(60, -40.3) * mm});
            skArc(sketch, "E80.4", {"start": v(-56.15, -48.18) * mm, "mid": v(0, -67.5) * mm, "end": v(56.15, -48.18) * mm});
            skLineSegment(sketch, "E80.5", {"start": v(-60, 40.3) * mm, "end": v(-60, -40.3) * mm});
            skArc(sketch, "E80.6", {"start": v(-56.15, 48.18) * mm, "mid": v(-58.99, 44.68) * mm, "end": v(-60, 40.3) * mm});
            skArc(sketch, "E80.7", {"start": v(-60, -40.3) * mm, "mid": v(-58.99, -44.68) * mm, "end": v(-56.15, -48.18) * mm});
            skLineSegment(sketch, "E81", {"start": v(0, 90) * mm, "end": v(0, 120) * mm, "construction": true});
            skCircle(sketch, "E82", {"center": v(0, 120) * mm, "radius": 6 * mm});
            skLineSegment(sketch, "E83", {"start": v(-33, 90) * mm, "end": v(-15, 108) * mm});
            skLineSegment(sketch, "E84", {"start": v(-15, 108) * mm, "end": v(-15, 120) * mm});
            skArc(sketch, "E85", {"start": v(-15, 120) * mm, "mid": v(0, 135) * mm, "end": v(15, 120) * mm});
            skLineSegment(sketch, "E86", {"start": v(15, 120) * mm, "end": v(15, 108) * mm});
            skLineSegment(sketch, "E87", {"start": v(15, 108) * mm, "end": v(33, 90) * mm});
            skLineSegment(sketch, "E88", {"start": v(-80, 0) * mm, "end": v(80, 0) * mm});
            skLineSegment(sketch, "E89.MirrorCS", {"start": v(-33, -90) * mm, "end": v(-15, -108) * mm});
            skLineSegment(sketch, "E90.MirrorCS", {"start": v(-15, -108) * mm, "end": v(-15, -120) * mm});
            skArc(sketch, "E91.MirrorCS", {"start": v(-15, -120) * mm, "mid": v(0, -135) * mm, "end": v(15, -120) * mm});
            skLineSegment(sketch, "E92.MirrorCS", {"start": v(15, -120) * mm, "end": v(15, -108) * mm});
            skLineSegment(sketch, "E93.MirrorCS", {"start": v(15, -108) * mm, "end": v(33, -90) * mm});
            skCircle(sketch, "E94.MirrorC", {"center": v(0, -120) * mm, "radius": 6 * mm});
            skSolve(sketch);
        }
        {
            var Q0;
            Q0=makeQuery(id+"F16.imprint","IMPRINT",FACE,{"disambiguationData":[TD([[makeQuery(id+"F16.imprint","IMPRINT",EDGE,{"derivedFrom":sQuery(id+"F16.wireOp",EDGE,"E82")}),-1.0]])]});
            var Q1;
            {var subQ8=sQuery(id+"F16.wireOp",EDGE,"E79.1");Q1=makeQuery(id+"F16.imprint","IMPRINT",FACE,{"disambiguationData":[TD([[makeQuery(id+"F16.imprint","IMPRINT",EDGE,{"derivedFrom":subQ8}),1.0]])]});}
            var Q2;
            {var subQ6=sQuery(id+"F16.wireOp",EDGE,"E79.5");Q2=makeQuery(id+"F16.imprint","IMPRINT",FACE,{"disambiguationData":[TD([[makeQuery(id+"F16.imprint","IMPRINT",EDGE,{"derivedFrom":subQ6}),1.0]])]});}
            var Q3;
            {var subQ0=sQuery(id+"F16.wireOp",EDGE,"E89.MirrorCS");Q3=makeQuery(id+"F16.imprint","IMPRINT",FACE,{"disambiguationData":[TD([[makeQuery(id+"F16.imprint","IMPRINT",EDGE,{"derivedFrom":subQ0}),1.0]])]});}
            var Q4;
            Q4=makeQuery(id+"F2.opExtrude","CAP_FACE",FACE,{"disambiguationData":[OSD([sQuery(id+"F0.wireOp",EDGE,"E12"),sQuery(id+"F0.wireOp",EDGE,"E13"),sQuery(id+"F0.wireOp",EDGE,"E14"),sQuery(id+"F0.wireOp",EDGE,"E15"),sQuery(id+"F0.wireOp",EDGE,"E17.filletArc"),sQuery(id+"F0.wireOp",EDGE,"E18.filletArc"),sQuery(id+"F0.wireOp",EDGE,"E19.filletArc"),sQuery(id+"F0.wireOp",EDGE,"E20.filletArc"),sQuery(id+"F0.wireOp",EDGE,"E25.0"),sQuery(id+"F0.wireOp",EDGE,"E25.1"),sQuery(id+"F0.wireOp",EDGE,"E25.2"),sQuery(id+"F0.wireOp",EDGE,"E25.3"),sQuery(id+"F0.wireOp",EDGE,"E25.4"),sQuery(id+"F0.wireOp",EDGE,"E25.5"),sQuery(id+"F0.wireOp",EDGE,"E25.6"),sQuery(id+"F0.wireOp",EDGE,"E25.7")])],"isStart":false});
            extrude(context, id + "F17", {"entities" : qUnion([Q0, Q1, Q2, Q3]), "endBound" : BoundingType.UP_TO_SURFACE, "endBoundEntityFace" : qUnion([Q4]), "depth" : 25 * mm});
        }
    });
